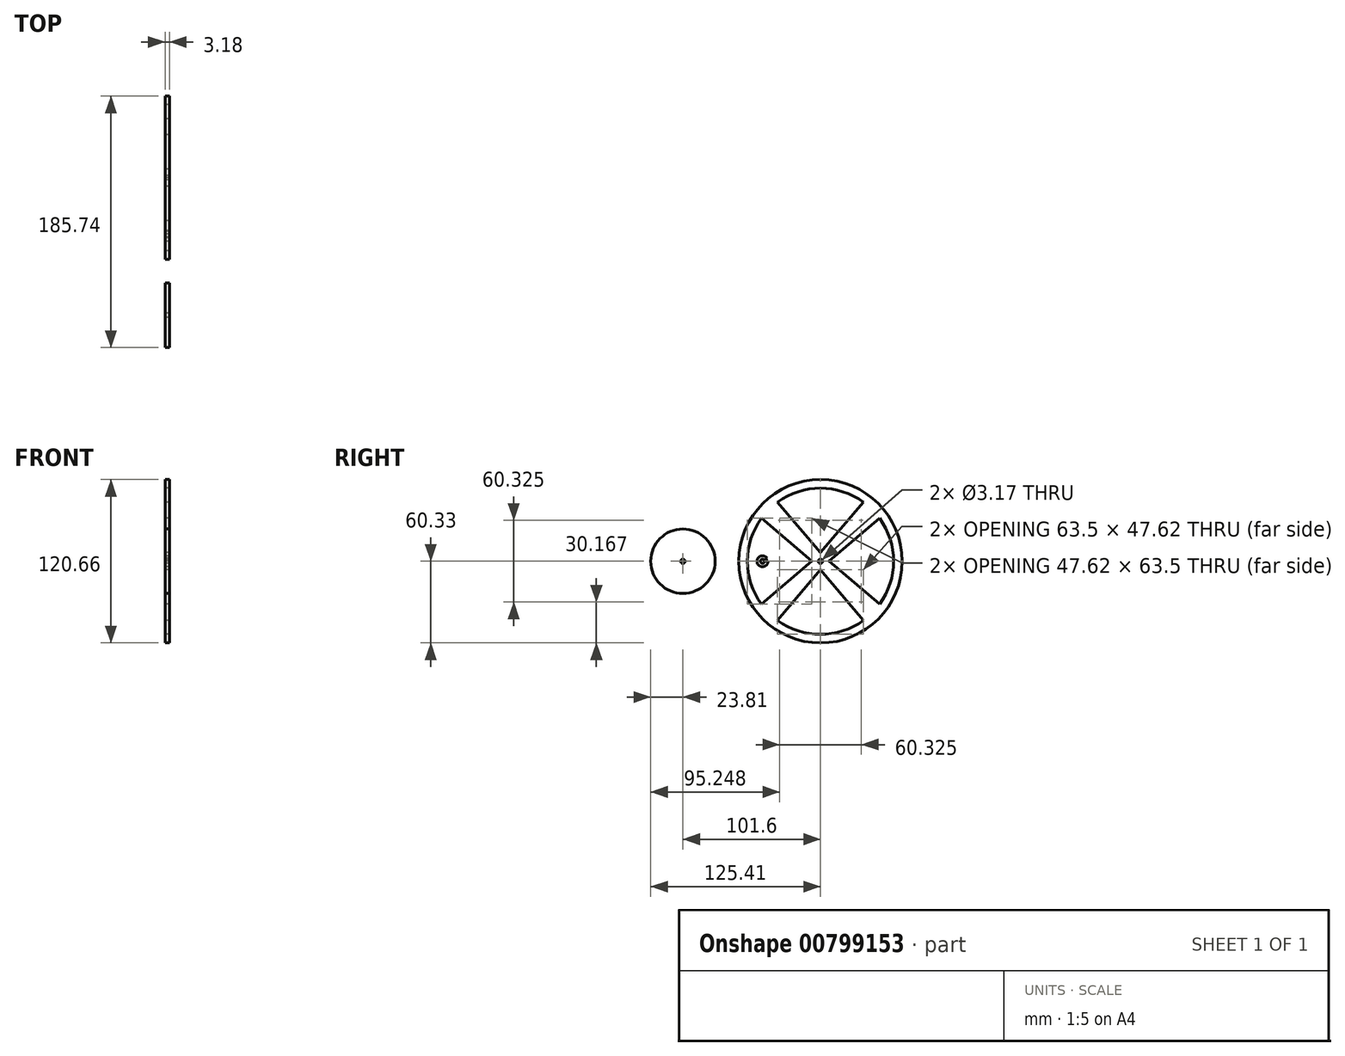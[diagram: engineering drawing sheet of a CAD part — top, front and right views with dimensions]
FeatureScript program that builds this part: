
annotation { "Feature Type Name" : "Feature", "Feature Type Description" : "" }
export const myFeature = defineFeature(function(context is Context, id is Id, definition is map)
    precondition{}
    {
        {
            var Q0;
            Q0=qCreatedBy(makeId("Right.planeOp"),FACE);
            var sketch = newSketch(context, id + "F0", { "sketchPlane" : qUnion([Q0])});
            skCircle(sketch, "E0", {"center": v(0, 0) * mm, "radius": 60.33 * mm});
            skCircle(sketch, "E1", {"center": v(0, 0) * mm, "radius": 53.98 * mm, "construction": true});
            skCircle(sketch, "E2", {"center": v(0, 0) * mm, "radius": 6.35 * mm, "construction": true});
            skArc(sketch, "E3", {"start": v(-31.75, 43.65) * mm, "mid": v(0, 53.98) * mm, "end": v(31.75, 43.65) * mm});
            skLineSegment(sketch, "E4", {"start": v(-31.75, 43.65) * mm, "end": v(0, 6.35) * mm});
            skLineSegment(sketch, "E5", {"start": v(0, 6.35) * mm, "end": v(31.75, 43.65) * mm});
            skArc(sketch, "E6", {"start": v(28.11, 46.07) * mm, "mid": v(38.17, 38.17) * mm, "end": v(46.07, 28.11) * mm});
            skArc(sketch, "E7", {"start": v(43.65, 31.75) * mm, "mid": v(53.98, 0) * mm, "end": v(43.65, -31.75) * mm});
            skLineSegment(sketch, "E8", {"start": v(43.65, 31.75) * mm, "end": v(6.35, 0) * mm});
            skLineSegment(sketch, "E9", {"start": v(6.35, 0) * mm, "end": v(43.65, -31.75) * mm});
            skArc(sketch, "E10", {"start": v(46.07, -28.11) * mm, "mid": v(38.17, -38.17) * mm, "end": v(28.11, -46.07) * mm});
            skArc(sketch, "E11", {"start": v(31.75, -43.65) * mm, "mid": v(0, -53.98) * mm, "end": v(-31.75, -43.65) * mm});
            skArc(sketch, "E12", {"start": v(-28.11, -46.07) * mm, "mid": v(-38.17, -38.17) * mm, "end": v(-46.07, -28.11) * mm});
            skArc(sketch, "E13", {"start": v(-43.65, -31.75) * mm, "mid": v(-53.98, 0) * mm, "end": v(-43.65, 31.75) * mm});
            skArc(sketch, "E14", {"start": v(-46.07, 28.11) * mm, "mid": v(-38.17, 38.17) * mm, "end": v(-28.11, 46.07) * mm});
            skLineSegment(sketch, "E15", {"start": v(31.75, -43.65) * mm, "end": v(0, -6.35) * mm});
            skLineSegment(sketch, "E16", {"start": v(0, -6.35) * mm, "end": v(-31.75, -43.65) * mm});
            skLineSegment(sketch, "E17", {"start": v(-43.65, -31.75) * mm, "end": v(-6.35, 0) * mm});
            skLineSegment(sketch, "E18", {"start": v(-6.35, 0) * mm, "end": v(-43.65, 31.75) * mm});
            skCircle(sketch, "E19", {"center": v(0, 0) * mm, "radius": 1.59 * mm});
            skSolve(sketch);
        }
        {
            var Q0;
            Q0 = qSketchRegion(id + "F0", true);
            var Q1;
            {var subQ6=sQuery(id+"F0.wireOp",EDGE,"E4");Q1=makeQuery(id+"F0.imprint","IMPRINT",FACE,{"disambiguationData":[TD([[makeQuery(id+"F0.imprint","IMPRINT",EDGE,{"derivedFrom":subQ6}),-1.0]])]});}
            extrude(context, id + "F1", {"entities" : qUnion([Q0, Q1]), "depth" : 3.17 * mm, "offsetDistance" : 25.4 * mm});
        }
        {
            var Q0;
            Q0=qCreatedBy(makeId("Right.planeOp"),FACE);
            var sketch = newSketch(context, id + "F2", { "sketchPlane" : qUnion([Q0])});
            skCircle(sketch, "E20", {"center": v(-101.6, 0) * mm, "radius": 23.81 * mm});
            skCircle(sketch, "E21", {"center": v(-101.6, 0) * mm, "radius": 1.59 * mm});
            skSolve(sketch);
        }
        {
            var Q0;
            Q0=makeQuery(id+"F2.imprint","IMPRINT",FACE,{"disambiguationData":[TD([[makeQuery(id+"F2.imprint","IMPRINT",EDGE,{"derivedFrom":sQuery(id+"F2.wireOp",EDGE,"E20")}),1.0]])]});
            extrude(context, id + "F3", {"entities" : qUnion([Q0]), "depth" : 3.17 * mm, "offsetDistance" : 25.4 * mm});
        }
        {
            var Q0;
            Q0=qCreatedBy(makeId("Right.planeOp"),FACE);
            var sketch = newSketch(context, id + "F4", { "sketchPlane" : qUnion([Q0])});
            skCircle(sketch, "E22", {"center": v(-42.86, 0) * mm, "radius": 1.52 * mm});
            skCircle(sketch, "E23", {"center": v(-42.86, 0) * mm, "radius": 4.06 * mm});
            skLineSegment(sketch, "E24", {"start": v(-41.64, 0.9) * mm, "end": v(-39.6, 2.41) * mm});
            skLineSegment(sketch, "E25", {"start": v(-41.34, 0) * mm, "end": v(-38.8, 0) * mm});
            skSolve(sketch);
        }
        {
            var Q0;
            {var subQ0=sQuery(id+"F4.wireOp",EDGE,"E24");Q0=makeQuery(id+"F4.imprint","IMPRINT",FACE,{"disambiguationData":[TD([[makeQuery(id+"F4.imprint","IMPRINT",EDGE,{"derivedFrom":subQ0}),1.0]])]});}
            extrude(context, id + "F5", {"entities" : qUnion([Q0]), "depth" : 3.17 * mm, "offsetDistance" : 25.4 * mm});
        }
    });
